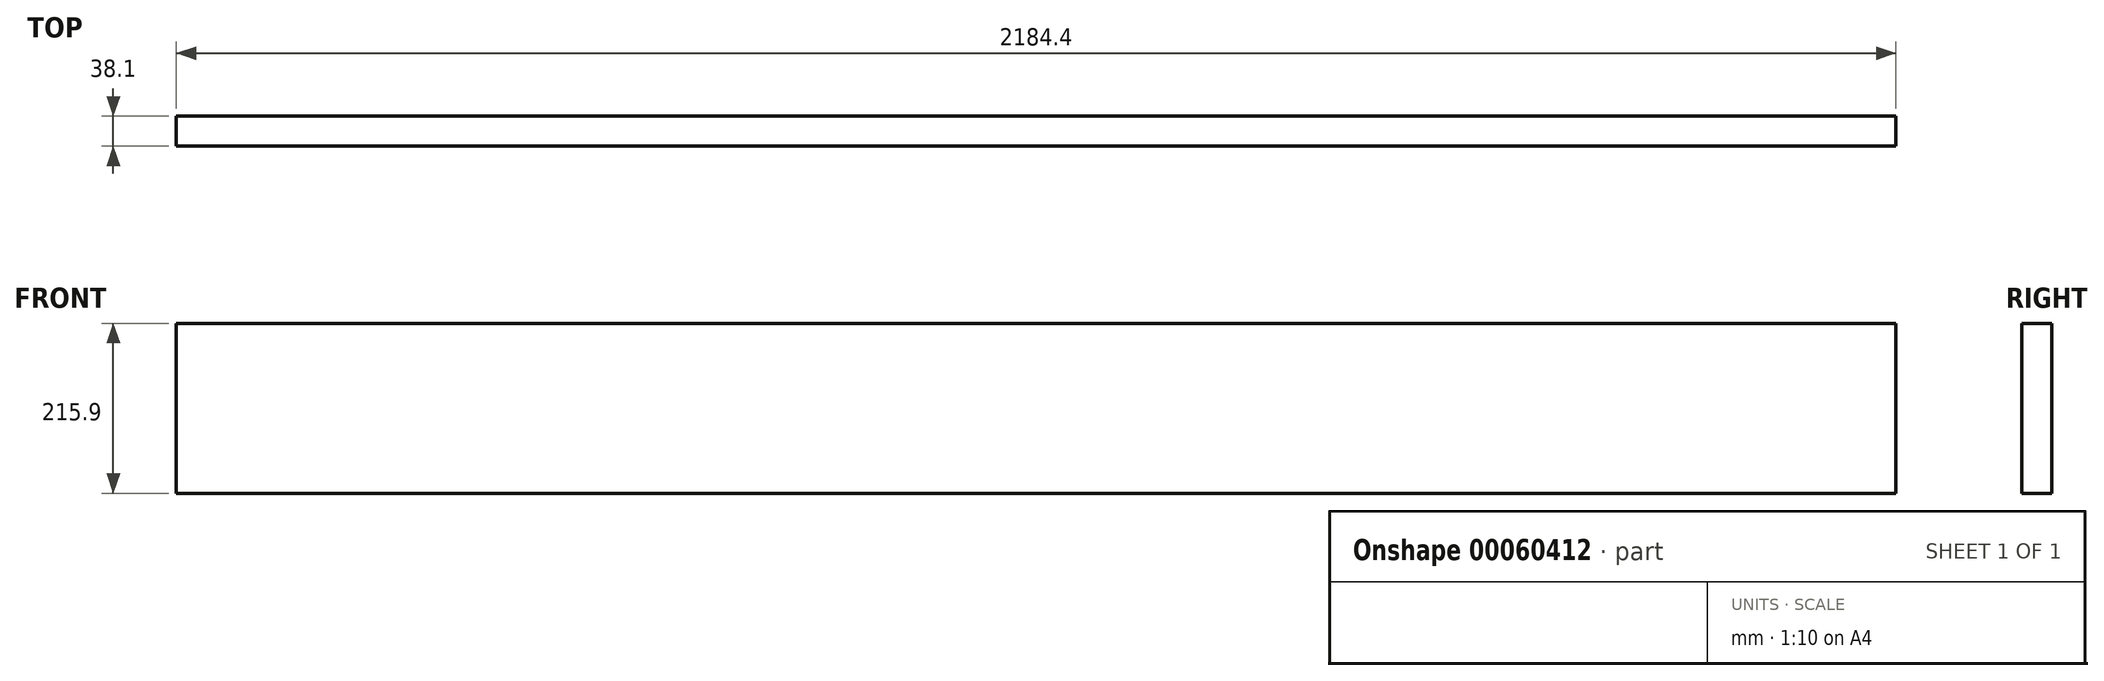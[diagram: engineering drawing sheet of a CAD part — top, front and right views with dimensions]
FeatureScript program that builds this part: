
annotation { "Feature Type Name" : "Feature", "Feature Type Description" : "" }
export const myFeature = defineFeature(function(context is Context, id is Id, definition is map)
    precondition{}
    {
        {
            var Q0;
            Q0=qCreatedBy(makeId("Right.planeOp"),FACE);
            var sketch = newSketch(context, id + "F0", { "sketchPlane" : qUnion([Q0])});
            skLineSegment(sketch, "E0.bottom", {"start": v(0, 0) * mm, "end": v(-38.1, 0) * mm});
            skLineSegment(sketch, "E0.top", {"start": v(0, 215.9) * mm, "end": v(-38.1, 215.9) * mm});
            skLineSegment(sketch, "E0.left", {"start": v(0, 0) * mm, "end": v(0, 215.9) * mm});
            skLineSegment(sketch, "E0.right", {"start": v(-38.1, 0) * mm, "end": v(-38.1, 215.9) * mm});
            skSolve(sketch);
        }
        {
            var Q0;
            Q0=makeQuery(id+"F0.imprint","IMPRINT",FACE,{"disambiguationData":[TD([[makeQuery(id+"F0.imprint","IMPRINT",EDGE,{"derivedFrom":sQuery(id+"F0.wireOp",EDGE,"E0.bottom")}),-1.0]])]});
            extrude(context, id + "F1", {"entities" : qUnion([Q0]), "depth" : 2184.4 * mm});
        }
    });
